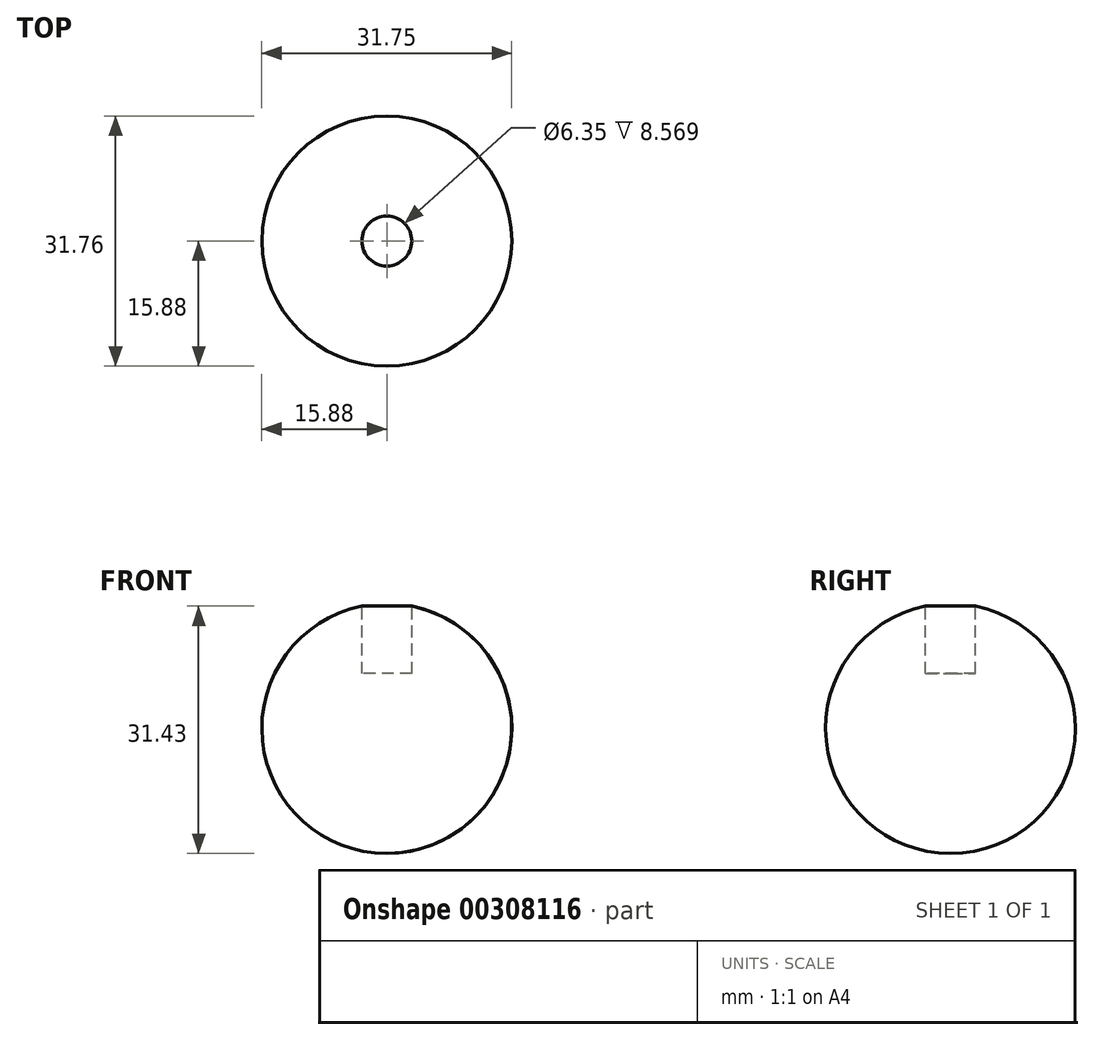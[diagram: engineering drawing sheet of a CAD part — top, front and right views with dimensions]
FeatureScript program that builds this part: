
annotation { "Feature Type Name" : "Feature", "Feature Type Description" : "" }
export const myFeature = defineFeature(function(context is Context, id is Id, definition is map)
    precondition{}
    {
        {
            var Q0;
            Q0=qCreatedBy(makeId("Front.planeOp"),FACE);
            var sketch = newSketch(context, id + "F0", { "sketchPlane" : qUnion([Q0])});
            skArc(sketch, "E0", {"start": v(0, 15.88) * mm, "mid": v(-15.88, 0) * mm, "end": v(0, -15.88) * mm});
            skLineSegment(sketch, "E1", {"start": v(0, 15.88) * mm, "end": v(0, -15.88) * mm});
            skSolve(sketch);
        }
        {
            var Q0;
            Q0=qCreatedBy(makeId("Top.planeOp"),FACE);
            var sketch = newSketch(context, id + "F1", { "sketchPlane" : qUnion([Q0])});
            skCircle(sketch, "E2", {"center": v(0, 0) * mm, "radius": 15.88 * mm});
            skSolve(sketch);
        }
        {
            var Q0;
            Q0=makeQuery(id+"F0.imprint","IMPRINT",FACE,{"disambiguationData":[TD([[makeQuery(id+"F0.imprint","IMPRINT",EDGE,{"derivedFrom":sQuery(id+"F0.wireOp",EDGE,"E0")}),1.0]])]});
            var Q1;
            Q1=sQuery(id+"F1.wireOp",EDGE,"E2");
            revolve(context, id + "F2", {"entities" : qUnion([Q0]), "axis" : qUnion([Q1]), "revolveType" : RevolveType.FULL});
        }
        {
            var Q0;
            Q0=qCreatedBy(makeId("Top.planeOp"),FACE);
            cPlane(context, id + "F3", {"entities" : qUnion([Q0]), "cplaneType" : CPlaneType.OFFSET, "offset" : 16.5 * mm, "width" : 152.4 * mm, "height" : 152.4 * mm});
        }
        {
            var Q0;
            Q0=qCreatedBy(id+"F3.planeOp",FACE);
            var sketch = newSketch(context, id + "F4", { "sketchPlane" : qUnion([Q0])});
            skCircle(sketch, "E3", {"center": v(0, 0) * mm, "radius": 3.18 * mm});
            skSolve(sketch);
        }
        {
            var Q0;
            Q0 = qSketchRegion(id + "F4", true);
            extrude(context, id + "F5", {"entities" : qUnion([Q0]), "operationType" : NewBodyOperationType.REMOVE, "oppositeDirection" : true, "depth" : 9.52 * mm});
        }
    });
